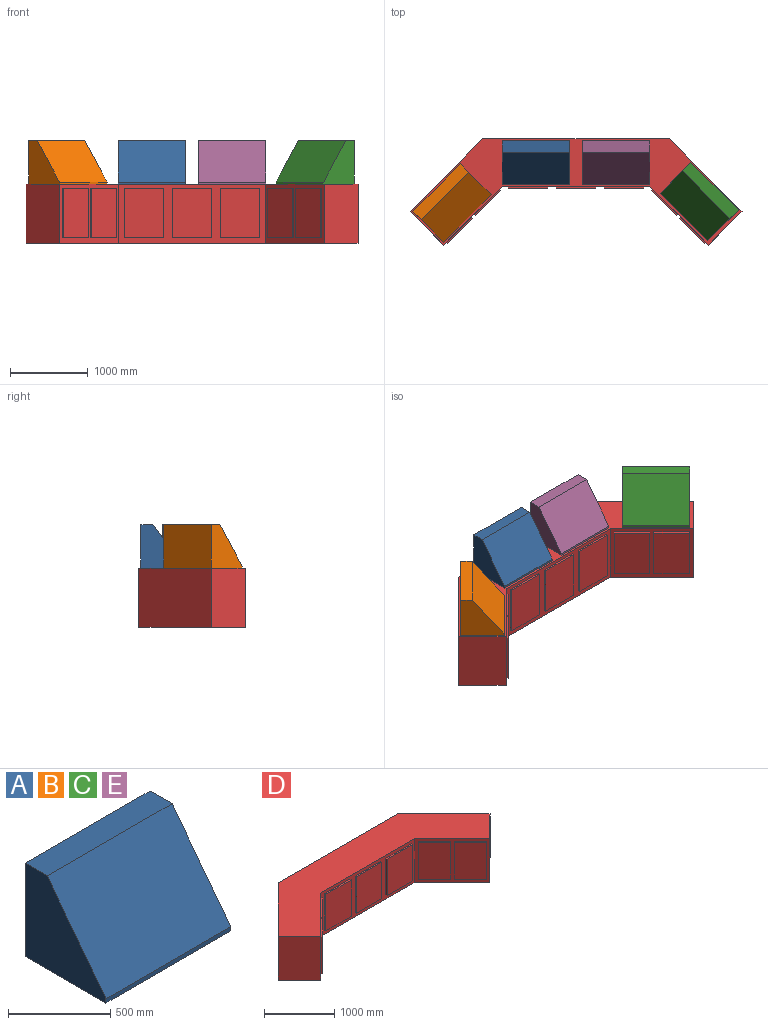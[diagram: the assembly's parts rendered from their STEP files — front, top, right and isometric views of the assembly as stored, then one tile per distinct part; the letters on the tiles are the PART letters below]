
ASSEMBLY  parts=5 mates=8
PART A: 7 faces, bbox 863.6x558.8x558.8 mm
  f0: plane 863.6x25.4mm, normal (0,-1,0), area 21935.4mm2, adj f1,f4,f5,f6
  f1: plane 863.6x558.8mm, normal (0,0,-1), area 482579.7mm2, adj f0,f2,f5,f6
  f2: plane 863.6x558.8mm, normal (0,1,0), area 482579.7mm2, adj f1,f3,f5,f6
  f3: plane 863.6x152.4mm, normal (0,0,1), area 131612.6mm2, adj f2,f4,f5,f6
  f4: plane 863.6x533.4mm, normal (0,-0.8,0.61), area 579112.2mm2, adj f0,f3,f5,f6
  f5: plane 558.8x558.8mm, normal (1,0,0), area 203870.6mm2, adj f0,f1,f2,f3,f4
  f6: plane 558.8x558.8mm, normal (-1,0,0), area 203870.6mm2, adj f0,f1,f2,f3,f4
PART B: same geometry as A
PART C: same geometry as A
PART D: 45 faces, bbox 4267.2x1365.3x762 mm
  f0: plane 762x755.67mm, normal (-0.71,-0.71,0), area 233252.4mm2, adj f5,f6,f8,f9,f20,f21,f22,f23
  f1: plane 762x755.67mm, normal (0.71,-0.71,0), area 233252.4mm2, adj f4,f5,f8,f9,f10,f11,f12,f13
  f2: plane 2400.3x762mm, normal (0,1,0), area 1829028.6mm2, adj f3,f7,f8,f9
  f3: plane 934.44x933.45mm, normal (-0.71,0.71,0), area 1006449.6mm2, adj f2,f4,f8,f9
  f4: plane 762x431.28mm, normal (-0.71,-0.71,0), area 464515.2mm2, adj f1,f3,f8,f9
  f5: plane 1894.91x762mm, normal (0,-1,0), area 476182.3mm2, adj f0,f1,f8,f9,f30,f31,f32,f33
  f6: plane 762x431.28mm, normal (0.71,-0.71,0), area 464515.2mm2, adj f0,f7,f8,f9
  f7: plane 934.44x933.45mm, normal (0.71,0.71,0), area 1006449.6mm2, adj f2,f6,f8,f9
  f8: plane 4267.2x1365.27mm, normal (0,0,1), area 2765457.2mm2, adj f0,f1,f2,f3,f4,f5,f6,f7
  f9: plane 4267.2x1365.27mm, normal (0,0,-1), area 2765457.2mm2, adj f0,f1,f2,f3,f4,f5,f6,f7
  f10: plane 635x17.97mm, normal (-0.71,-0.71,0), area 16129mm2, adj f1,f11,f13,f14
  f11: plane 341.41x341.09mm, normal (0,0,-1), area 11612.9mm2, adj f1,f10,f12,f14
  f12: plane 635x17.97mm, normal (0.71,0.71,0), area 16129mm2, adj f1,f11,f13,f14
  f13: plane 341.41x341.09mm, normal (0,0,1), area 11612.9mm2, adj f1,f10,f12,f14
  f14: plane 635x323.46mm, normal (0.71,-0.71,0), area 290322mm2, adj f10,f11,f12,f13
  f15: plane 635x17.97mm, normal (0.71,0.71,0), area 16129mm2, adj f1,f16,f18,f19
  f16: plane 341.41x341.09mm, normal (0,0,1), area 11612.9mm2, adj f1,f15,f17,f19
  f17: plane 635x17.97mm, normal (-0.71,-0.71,0), area 16129mm2, adj f1,f16,f18,f19
  f18: plane 341.41x341.09mm, normal (0,0,-1), area 11612.9mm2, adj f1,f15,f17,f19
  f19: plane 635x323.46mm, normal (0.71,-0.71,0), area 290322mm2, adj f15,f16,f17,f18
  f20: plane 635x17.97mm, normal (-0.71,0.71,0), area 16129mm2, adj f0,f21,f23,f24
  f21: plane 341.41x341.09mm, normal (0,0,-1), area 11612.9mm2, adj f0,f20,f22,f24
  f22: plane 635x17.97mm, normal (0.71,-0.71,0), area 16129mm2, adj f0,f21,f23,f24
  f23: plane 341.41x341.09mm, normal (0,0,1), area 11612.9mm2, adj f0,f20,f22,f24
  f24: plane 635x323.46mm, normal (-0.71,-0.71,0), area 290322mm2, adj f20,f21,f22,f23
  f25: plane 635x17.97mm, normal (0.71,-0.71,0), area 16129mm2, adj f0,f26,f28,f29
  f26: plane 341.41x341.09mm, normal (0,0,1), area 11612.9mm2, adj f0,f25,f27,f29
  f27: plane 635x17.97mm, normal (-0.71,0.71,0), area 16129mm2, adj f0,f26,f28,f29
  f28: plane 341.41x341.09mm, normal (0,0,-1), area 11612.9mm2, adj f0,f25,f27,f29
  f29: plane 635x323.46mm, normal (-0.71,-0.71,0), area 290322mm2, adj f25,f26,f27,f28
  f30: plane 635x25.4mm, normal (-1,0,0), area 16129mm2, adj f5,f31,f33,f34
  f31: plane 508x25.4mm, normal (0,0,-1), area 12903.2mm2, adj f5,f30,f32,f34
  f32: plane 635x25.4mm, normal (1,0,0), area 16129mm2, adj f5,f31,f33,f34
  f33: plane 508x25.4mm, normal (0,0,1), area 12903.2mm2, adj f5,f30,f32,f34
  f34: plane 635x508mm, normal (0,-1,0), area 322580mm2, adj f30,f31,f32,f33
  f35: plane 635x25.4mm, normal (-1,0,0), area 16129mm2, adj f5,f36,f38,f39
  f36: plane 508x25.4mm, normal (0,0,-1), area 12903.2mm2, adj f5,f35,f37,f39
  f37: plane 635x25.4mm, normal (1,0,0), area 16129mm2, adj f5,f36,f38,f39
  f38: plane 508x25.4mm, normal (0,0,1), area 12903.2mm2, adj f5,f35,f37,f39
  f39: plane 635x508mm, normal (0,-1,0), area 322580mm2, adj f35,f36,f37,f38
  f40: plane 635x25.4mm, normal (-1,0,0), area 16129mm2, adj f5,f41,f43,f44
  f41: plane 508x25.4mm, normal (0,0,-1), area 12903.2mm2, adj f5,f40,f42,f44
  f42: plane 635x25.4mm, normal (1,0,0), area 16129mm2, adj f5,f41,f43,f44
  f43: plane 508x25.4mm, normal (0,0,1), area 12903.2mm2, adj f5,f40,f42,f44
  f44: plane 635x508mm, normal (0,-1,0), area 322580mm2, adj f40,f41,f42,f43
PART E: same geometry as A
PLACE A t=(-779.58,-9.82,873.87)mm
PLACE B rot(axis=(0,0,1),45deg) t=(-1708.8,-826.35,873.87)mm
PLACE C rot(axis=(0,0,-1),45deg) t=(1422.72,-197.25,873.87)mm
PLACE D t=(-779.58,-282.67,30.41)mm fixed
PLACE E t=(251.74,-9.82,873.87)mm
MATE parallel D.f3 <-> B.f2  axis (-0.71,0.71,0) through (-1499,-140.29,411.41)mm
MATE parallel C.f2 <-> D.f7  axis (0.71,0.71,0) through (1948.16,-282.7,1071.81)mm
MATE fastened E.f1 <-> D.f8  axis (0,0,1) through (1115.34,-282.67,792.41)mm
MATE parallel B.f6 <-> D.f4  axis (-0.71,-0.71,0) through (-1785.54,-749.69,1017.8)mm
MATE planar D.f8 <-> B.f1  axis (0,0,1) through (-1157.01,-660.51,792.41)mm
MATE fastened A.f1 <-> D.f8  axis (0,0,1) through (-779.58,-282.67,792.41)mm
MATE parallel D.f6 <-> C.f5  axis (0.71,-0.71,0) through (2085.84,-822.93,411.41)mm
MATE planar D.f8 <-> C.f1  axis (0,0,1) through (167.88,-189.88,792.41)mm
